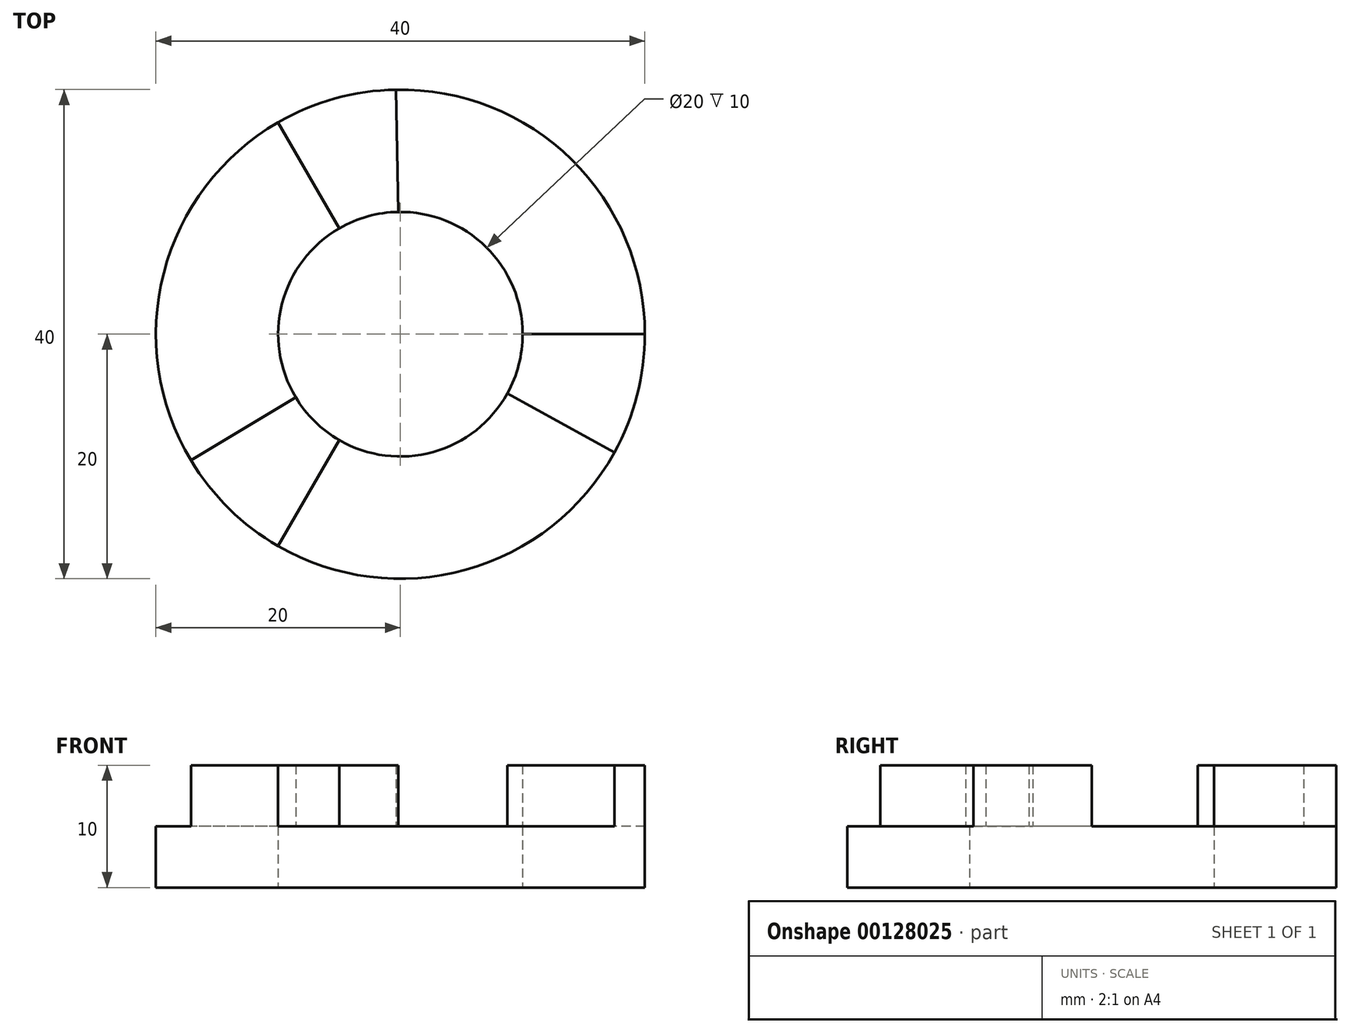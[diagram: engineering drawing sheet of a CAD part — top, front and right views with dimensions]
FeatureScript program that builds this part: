
annotation { "Feature Type Name" : "Feature", "Feature Type Description" : "" }
export const myFeature = defineFeature(function(context is Context, id is Id, definition is map)
    precondition{}
    {
        {
            var Q0;
            Q0=qCreatedBy(makeId("Top.planeOp"),FACE);
            var sketch = newSketch(context, id + "F0", { "sketchPlane" : qUnion([Q0])});
            skCircle(sketch, "E0", {"center": v(0, 0) * mm, "radius": 10 * mm});
            skCircle(sketch, "E1", {"center": v(0, 0) * mm, "radius": 20 * mm});
            skSolve(sketch);
        }
        {
            var Q0;
            Q0=qSketchRegion(id+"F0",true);
            extrude(context, id + "F1", {"entities" : qUnion([Q0]), "depth" : 5 * mm});
        }
        {
            var Q0;
            Q0=makeQuery(id+"F1.opExtrude","CAP_FACE",FACE,{"disambiguationData":[OSD([sQuery(id+"F0.wireOp",EDGE,"E0"),sQuery(id+"F0.wireOp",EDGE,"E1")])],"isStart":false});
            var sketch = newSketch(context, id + "F2", { "sketchPlane" : qUnion([Q0])});
            skLineSegment(sketch, "E2", {"start": v(0, 0) * mm, "end": v(0, 20) * mm, "construction": true});
            skLineSegment(sketch, "E3", {"start": v(0, 0) * mm, "end": v(-17.32, -10) * mm, "construction": true});
            skLineSegment(sketch, "E4", {"start": v(0, 0) * mm, "end": v(17.32, -10) * mm, "construction": true});
            skLineSegment(sketch, "E5", {"start": v(-8.57, -5.16) * mm, "end": v(-17.14, -10.31) * mm});
            skLineSegment(sketch, "E6", {"start": v(-5, -8.66) * mm, "end": v(-10, -17.32) * mm});
            skArc(sketch, "E7", {"start": v(-8.57, -5.16) * mm, "mid": v(-7, -7.14) * mm, "end": v(-5, -8.66) * mm});
            skArc(sketch, "E8", {"start": v(-17.14, -10.31) * mm, "mid": v(-14.01, -14.27) * mm, "end": v(-10, -17.32) * mm});
            skLineSegment(sketch, "E9.1.0", {"start": v(8.75, -4.84) * mm, "end": v(17.5, -9.68) * mm});
            skArc(sketch, "E9.1.1", {"start": v(8.75, -4.84) * mm, "mid": v(9.68, -2.5) * mm, "end": v(10, 0) * mm});
            skLineSegment(sketch, "E9.1.2", {"start": v(10, 0) * mm, "end": v(20, 0) * mm});
            skArc(sketch, "E9.1.3", {"start": v(17.5, -9.68) * mm, "mid": v(19.36, -5) * mm, "end": v(20, 0) * mm});
            skLineSegment(sketch, "E9.2.0", {"start": v(-0.18, 10) * mm, "end": v(-0.36, 20) * mm});
            skArc(sketch, "E9.2.1", {"start": v(-0.18, 10) * mm, "mid": v(-2.68, 9.64) * mm, "end": v(-5, 8.66) * mm});
            skLineSegment(sketch, "E9.2.2", {"start": v(-5, 8.66) * mm, "end": v(-10, 17.32) * mm});
            skArc(sketch, "E9.2.3", {"start": v(-0.36, 20) * mm, "mid": v(-5.35, 19.27) * mm, "end": v(-10, 17.32) * mm});
            skSolve(sketch);
        }
        {
            var Q0;
            Q0=qSketchRegion(id+"F2",true);
            extrude(context, id + "F3", {"entities" : qUnion([Q0]), "operationType" : NewBodyOperationType.ADD, "depth" : 5 * mm});
        }
    });
